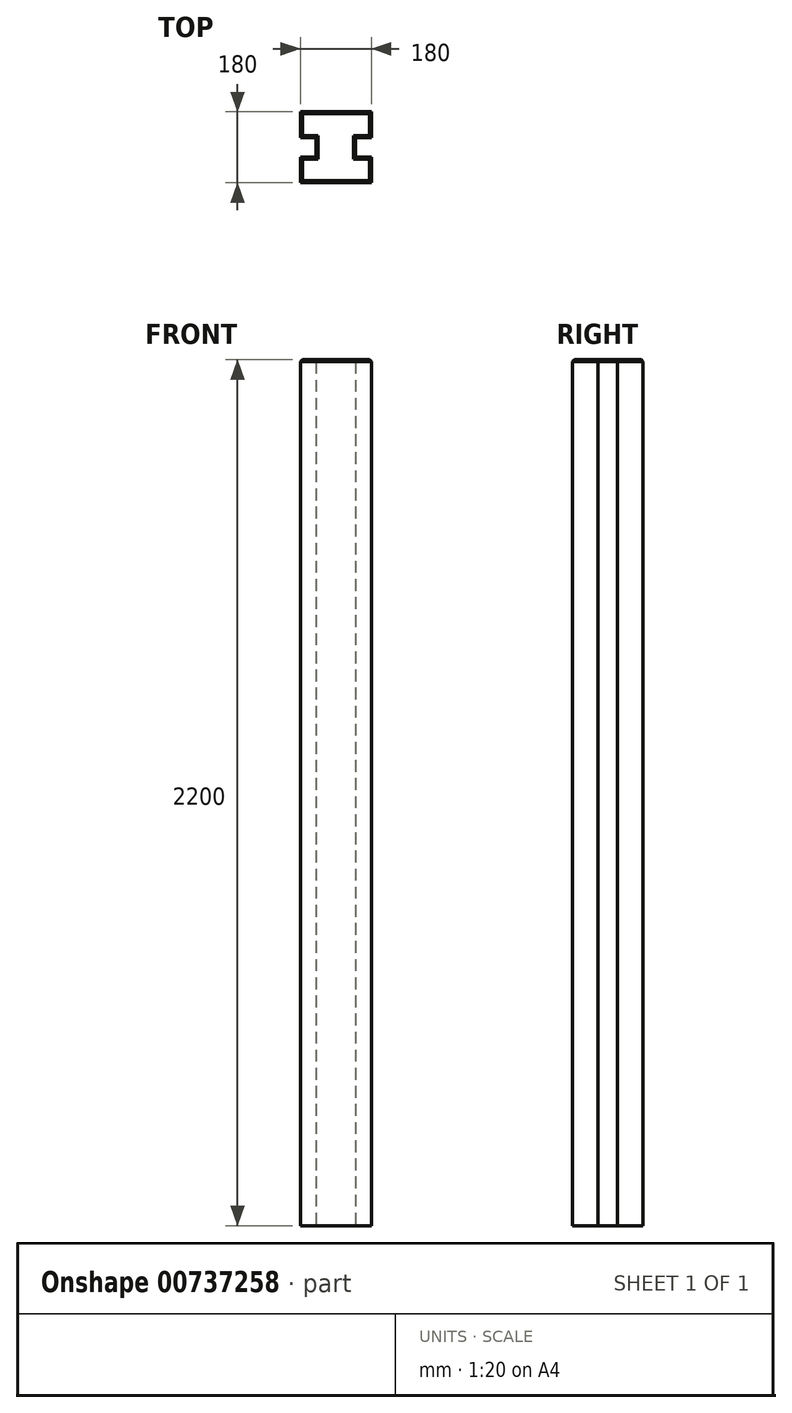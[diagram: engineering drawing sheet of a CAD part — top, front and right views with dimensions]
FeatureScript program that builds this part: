
annotation { "Feature Type Name" : "Feature", "Feature Type Description" : "" }
export const myFeature = defineFeature(function(context is Context, id is Id, definition is map)
    precondition{}
    {
        {
            var Q0;
            Q0=qCreatedBy(makeId("Top.planeOp"),FACE);
            var sketch = newSketch(context, id + "F0", { "sketchPlane" : qUnion([Q0])});
            skLineSegment(sketch, "E0.bottom", {"start": v(0, 0) * mm, "end": v(180, 0) * mm});
            skLineSegment(sketch, "E0.top", {"start": v(0, 180) * mm, "end": v(180, 180) * mm});
            skLineSegment(sketch, "E0.left", {"start": v(0, 0) * mm, "end": v(0, 65) * mm});
            skLineSegment(sketch, "E0.right", {"start": v(180, 0) * mm, "end": v(180, 65) * mm});
            skLineSegment(sketch, "E1.bottom", {"start": v(0, 115) * mm, "end": v(40, 115) * mm});
            skLineSegment(sketch, "E1.top", {"start": v(0, 65) * mm, "end": v(40, 65) * mm});
            skLineSegment(sketch, "E1.right", {"start": v(40, 115) * mm, "end": v(40, 65) * mm});
            skLineSegment(sketch, "E2.bottom", {"start": v(180, 115) * mm, "end": v(140, 115) * mm});
            skLineSegment(sketch, "E2.top", {"start": v(180, 65) * mm, "end": v(140, 65) * mm});
            skLineSegment(sketch, "E2.right", {"start": v(140, 115) * mm, "end": v(140, 65) * mm});
            skLineSegment(sketch, "E3.trimOffspring", {"start": v(0, 115) * mm, "end": v(0, 180) * mm});
            skLineSegment(sketch, "E4.trimOffspring", {"start": v(180, 115) * mm, "end": v(180, 180) * mm});
            skSolve(sketch);
        }
        {
            var Q0;
            Q0=makeQuery(id+"F0.imprint","IMPRINT",FACE,{"disambiguationData":[TD([[makeQuery(id+"F0.imprint","IMPRINT",EDGE,{"derivedFrom":sQuery(id+"F0.wireOp",EDGE,"E0.bottom")}),1.0]])]});
            extrude(context, id + "F1", {"entities" : qUnion([Q0]), "depth" : 2200 * mm, "offsetDistance" : 25 * mm});
        }
        {
            var Q0;
            Q0=makeQuery(id+"F1.opExtrude","CAP_EDGE",EDGE,{"disambiguationData":[OSD([sQuery(id+"F0.wireOp",EDGE,"E0.bottom")])],"isStart":false});
            var Q1;
            Q1=makeQuery(id+"F1.opExtrude","CAP_EDGE",EDGE,{"disambiguationData":[OSD([sQuery(id+"F0.wireOp",EDGE,"E0.left")])],"isStart":false});
            var Q2;
            Q2=makeQuery(id+"F1.opExtrude","CAP_EDGE",EDGE,{"disambiguationData":[OSD([sQuery(id+"F0.wireOp",EDGE,"E1.top")])],"isStart":false});
            var Q3;
            Q3=makeQuery(id+"F1.opExtrude","CAP_EDGE",EDGE,{"disambiguationData":[OSD([sQuery(id+"F0.wireOp",EDGE,"E1.right")])],"isStart":false});
            var Q4;
            Q4=makeQuery(id+"F1.opExtrude","CAP_EDGE",EDGE,{"disambiguationData":[OSD([sQuery(id+"F0.wireOp",EDGE,"E1.bottom")])],"isStart":false});
            var Q5;
            Q5=makeQuery(id+"F1.opExtrude","CAP_EDGE",EDGE,{"disambiguationData":[OSD([sQuery(id+"F0.wireOp",EDGE,"E3.trimOffspring")])],"isStart":false});
            var Q6;
            Q6=makeQuery(id+"F1.opExtrude","CAP_EDGE",EDGE,{"disambiguationData":[OSD([sQuery(id+"F0.wireOp",EDGE,"E0.top")])],"isStart":false});
            var Q7;
            Q7=makeQuery(id+"F1.opExtrude","CAP_EDGE",EDGE,{"disambiguationData":[OSD([sQuery(id+"F0.wireOp",EDGE,"E4.trimOffspring")])],"isStart":false});
            var Q8;
            Q8=makeQuery(id+"F1.opExtrude","CAP_EDGE",EDGE,{"disambiguationData":[OSD([sQuery(id+"F0.wireOp",EDGE,"E2.bottom")])],"isStart":false});
            var Q9;
            Q9=makeQuery(id+"F1.opExtrude","CAP_FACE",FACE,{"disambiguationData":[OSD([sQuery(id+"F0.wireOp",EDGE,"E0.bottom"),sQuery(id+"F0.wireOp",EDGE,"E0.top"),sQuery(id+"F0.wireOp",EDGE,"E0.left"),sQuery(id+"F0.wireOp",EDGE,"E0.right"),sQuery(id+"F0.wireOp",EDGE,"E1.bottom"),sQuery(id+"F0.wireOp",EDGE,"E1.top"),sQuery(id+"F0.wireOp",EDGE,"E1.right"),sQuery(id+"F0.wireOp",EDGE,"E2.bottom"),sQuery(id+"F0.wireOp",EDGE,"E2.top"),sQuery(id+"F0.wireOp",EDGE,"E2.right"),sQuery(id+"F0.wireOp",EDGE,"E3.trimOffspring"),sQuery(id+"F0.wireOp",EDGE,"E4.trimOffspring")])],"isStart":false});
            chamfer(context, id + "F2", {"entities" : qUnion([Q0, Q1, Q2, Q3, Q4, Q5, Q6, Q7, Q8, Q9]), "width" : 5 * mm, "tangentPropagation" : true});
        }
    });
